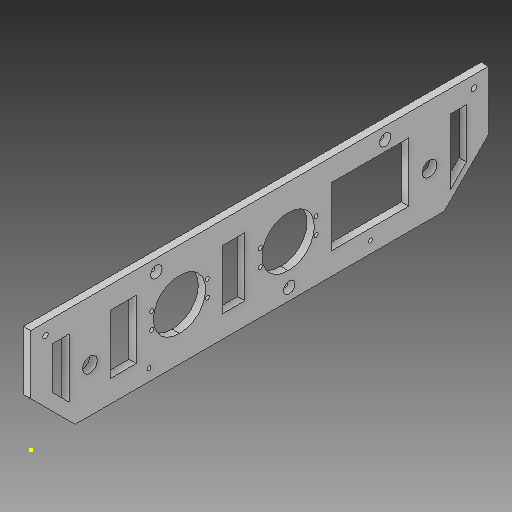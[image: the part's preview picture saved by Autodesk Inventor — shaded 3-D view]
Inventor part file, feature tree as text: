
AUTODESK INVENTOR PART (.ipt)
format: ipt  version: 2017 (Build 210142000, 142)  size: 303,104 bytes
history: native  units: in
note: dims shown in document units (in); Inventor stores cm internally (conversion verified against a paired STEP export)
features: sketch x15, hole x8, extrude x7, chamfer x3, thicken_offset x1, projected_geometry x1
ambient origin geometry x8: Origin, YZ Plane, XZ Plane, XY Plane, X Axis, Y Axis, Z Axis, Center Point
bodies: Solid1 (feature_tree)
feature tree (35):
  extrude  "Extrusion1"  Depth=15.5in
  sketch  "Sketch3"  dims[d4=2.0in]
  sketch  "Sketch4"  dims[d5=1.0in]
  chamfer  "Chamfer1"  Distance=0.25in
  chamfer  "Chamfer2"  Distance=1.5in Angle=45.0deg
  hole  "Hole1"  [1 undecoded]
  hole  "Hole3"  [1 undecoded]
  sketch  "Sketch8"  dims[d13=1.5in d14=0.125in d15=45.0deg d16=2.0in]
  hole  "Hole4"  [1 undecoded]
  hole  "Hole6"  [1 undecoded]
  extrude  "Extrusion2"  Depth=0.5in
  thicken_offset  "Thicken1"
  sketch  "Sketch16"  dims[d20=0.501in d21=0.75in d22=0.375in d23=0.25in d24=0.5635in d25=1.0in d26=0.8108in d42=0.394in]
  sketch  "Sketch17"  dims[d43=3.75in d44=3.75in]
  sketch  "Sketch18"  dims[d45=0.144in d46=0.5in]
  hole  "Hole10"  [1 undecoded]
  hole  "Hole11"  [1 undecoded]
  hole  "Hole12"  [1 undecoded]
  hole  "Hole13"  [1 undecoded]
  sketch  "Sketch19"  dims[d47=0.5in]
  sketch  "Sketch20"  dims[d48=0.188in d49=0.75in d50=0.375in d51=0.25in d52=0.5635in d53=1.0in d54=0.8108in d57=0.394in]
  extrude  "Extrusion3"  Depth=0.75in
  extrude  "Extrusion4"  Depth=0.75in
  sketch  "Sketch21"  dims[d61=0.14in d62=0.75in d63=0.375in d64=0.25in d65=0.5635in d66=1.0in d67=0.8108in]
  extrude  "Extrusion5"  Depth=0.75in
  extrude  "Extrusion6"  Depth=0.75in
  extrude  "Extrusion7"  Depth=0.75in
  chamfer  "Chamfer5"  Distance=0.945in
  sketch  "Sketch1"  dims[d2=3.25in d3=15.5in]
  sketch  "Sketch5"  dims[d6=2.0in]
  projected_geometry  "Projected Loop1"
  sketch  "Sketch7"  dims[d7=1.0in d8=0.25in d9=0.0in d10=1.5in d11=0.125in d12=45.0deg]
  sketch  "Sketch10"  dims[d17=1.5in d18=1.5in]
  sketch  "Sketch14"  dims[d19=2.0in]
  sketch  "Sketch22"  dims[d75=1.7in d76=0.75in d77=0.375in d78=0.25in d79=0.5635in d80=1.0in d81=0.8108in d82=0.144in d108=1.5in d109=1.5in d113=0.945in d114=0.276in d115=0.276in d116=0.945in d117=0.945in d118=0.945in d119=0.138in d120=0.138in d121=0.138in d122=0.138in d123=0.138in d124=1.0in d125=0.0in d128=8.75in d129=0.25in d130=0.25in d131=0.4in d132=0.4in d133=3.0in d135=0.14in d136=3.5in d138=0.14in d139=0.394in d141=4.0in d143=4.0in d145=0.188in d146=0.188in d147=0.14in d148=0.75in d149=0.375in d150=0.25in d151=0.5635in d152=1.0in d153=0.8108in d154=0.14in d155=0.75in d156=0.375in d157=0.25in d158=0.5635in d159=1.0in d160=0.8108in d161=0.14in d162=0.75in d163=0.375in d164=0.25in d165=0.5635in d166=1.0in d167=0.8108in d168=0.14in d169=0.75in d170=0.375in d171=0.25in d172=0.5635in d173=1.0in d174=0.8108in d183=0.75in d184=0.75in d185=0.75in d186=0.45in d187=0.45in d188=0.45in d189=0.45in d190=0.75in d191=1.0in d192=0.0in d193=1.0in d194=0.0in d195=0.75in d196=0.45in d197=0.45in d198=0.75in d199=0.75in d200=0.75in d201=0.45in d202=0.45in d203=1.0in d204=0.0in d205=1.0in d206=0.0in d207=0.75in d208=0.45in d209=0.75in d210=1.0in d211=0.0in d212=0.125in d213=0.125in d214=45.0deg d177=1.0in d178=1.0in]
note: 8 required parameter values undecoded (feature->parameter linkage not recoverable at this tier; creation-order binding heuristic only, values carry confidence <= 0.55)
